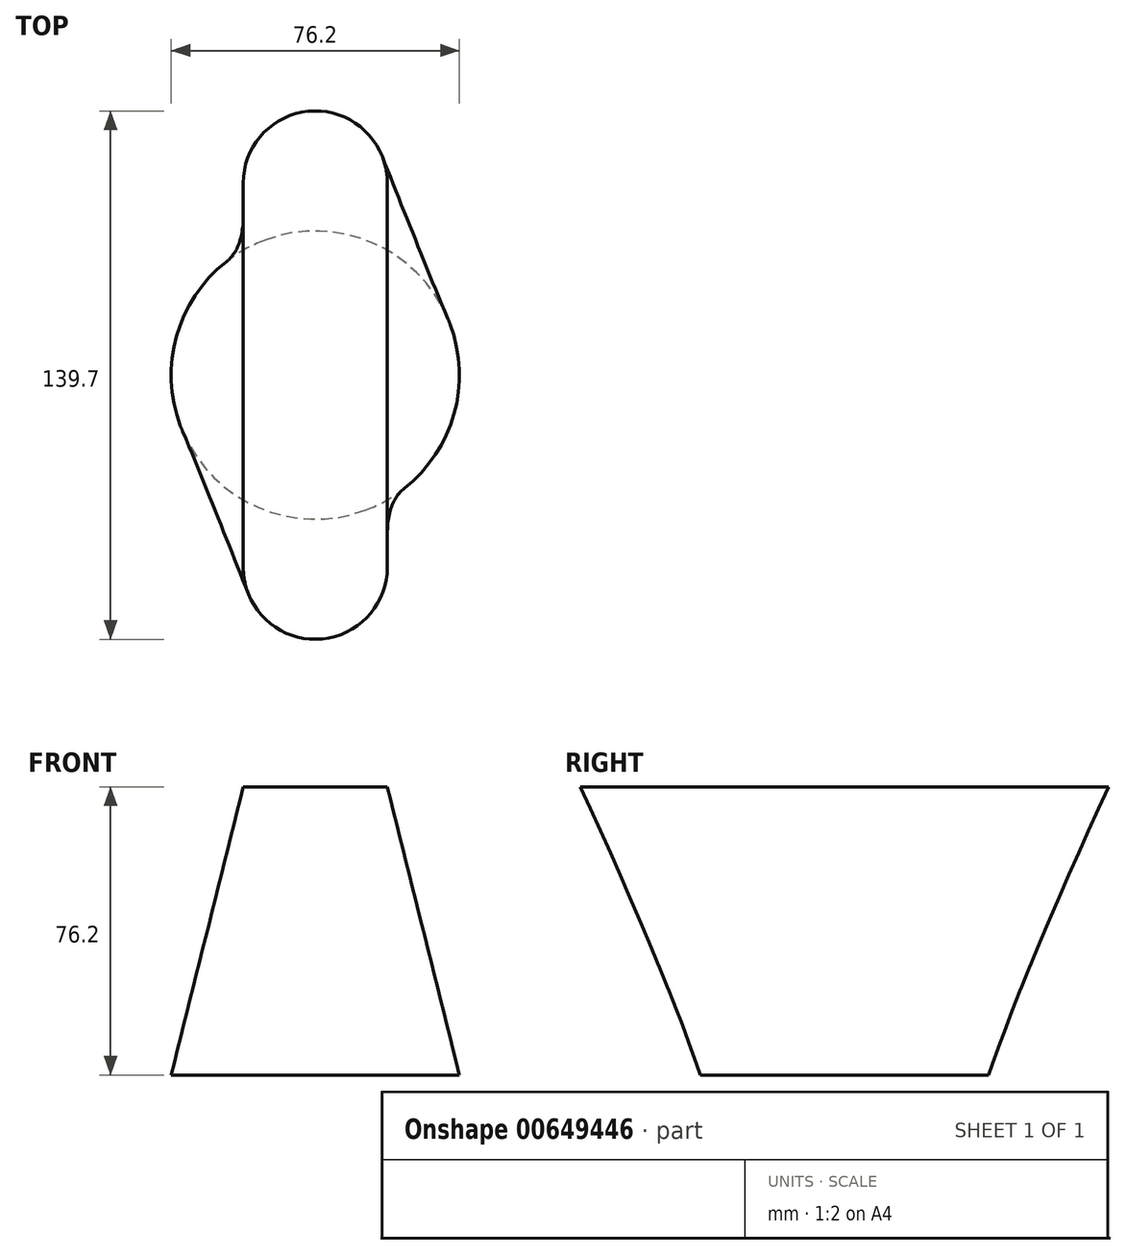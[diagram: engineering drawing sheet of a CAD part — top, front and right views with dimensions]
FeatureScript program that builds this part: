
annotation { "Feature Type Name" : "Feature", "Feature Type Description" : "" }
export const myFeature = defineFeature(function(context is Context, id is Id, definition is map)
    precondition{}
    {
        {
            var Q0;
            Q0=qCreatedBy(makeId("Top.planeOp"),FACE);
            var sketch = newSketch(context, id + "F0", { "sketchPlane" : qUnion([Q0])});
            skCircle(sketch, "E0", {"center": v(0, 0) * mm, "radius": 38.1 * mm});
            skSolve(sketch);
        }
        {
            var Q0;
            Q0=qCreatedBy(makeId("Top.planeOp"),FACE);
            var Q1;
            Q1 = qBodyType(qCreatedBy(id + "FiCFmErR0ERXYqn_0" ,EDGE), BodyType.WIRE);
            cPlane(context, id + "F1", {"entities" : qUnion([Q0, Q1]), "cplaneType" : CPlaneType.OFFSET, "offset" : 76.2 * mm, "width" : 152.4 * mm, "height" : 152.4 * mm});
        }
        {
            var Q0;
            Q0=qCreatedBy(id+"F1.planeOp",FACE);
            var sketch = newSketch(context, id + "F2", { "sketchPlane" : qUnion([Q0])});
            skLineSegment(sketch, "E1.bottom", {"start": v(19.05, -50.8) * mm, "end": v(-19.05, -50.8) * mm, "construction": true});
            skLineSegment(sketch, "E1.top", {"start": v(19.05, 50.8) * mm, "end": v(-19.05, 50.8) * mm, "construction": true});
            skLineSegment(sketch, "E1.left", {"start": v(19.05, -50.8) * mm, "end": v(19.05, 50.8) * mm});
            skLineSegment(sketch, "E1.right", {"start": v(-19.05, -50.8) * mm, "end": v(-19.05, 50.8) * mm});
            skPoint(sketch, "E1.middle", {"position": v(0, 0) * mm});
            skArc(sketch, "E2", {"start": v(19.05, 50.8) * mm, "mid": v(0, 69.85) * mm, "end": v(-19.05, 50.8) * mm});
            skArc(sketch, "E3", {"start": v(-19.05, -50.8) * mm, "mid": v(0, -69.85) * mm, "end": v(19.05, -50.8) * mm});
            skSolve(sketch);
        }
        {
            var Q0;
            Q0=makeQuery(id+"F0.imprint","IMPRINT",FACE,{"disambiguationData":[TD([[makeQuery(id+"F0.imprint","IMPRINT",EDGE,{"derivedFrom":sQuery(id+"F0.wireOp",EDGE,"E0")}),1.0]])]});
            var Q1;
            Q1=makeQuery(id+"F2.imprint","IMPRINT",FACE,{"disambiguationData":[TD([[makeQuery(id+"F2.imprint","IMPRINT",EDGE,{"derivedFrom":sQuery(id+"F2.wireOp",EDGE,"E1.left")}),1.0]])]});
            loft(context, id + "F3", {"sheetProfilesArray" : [{ "sheetProfileEntities" : qUnion([Q0]) }, { "sheetProfileEntities" : qUnion([Q1]) }]});
        }
    });
